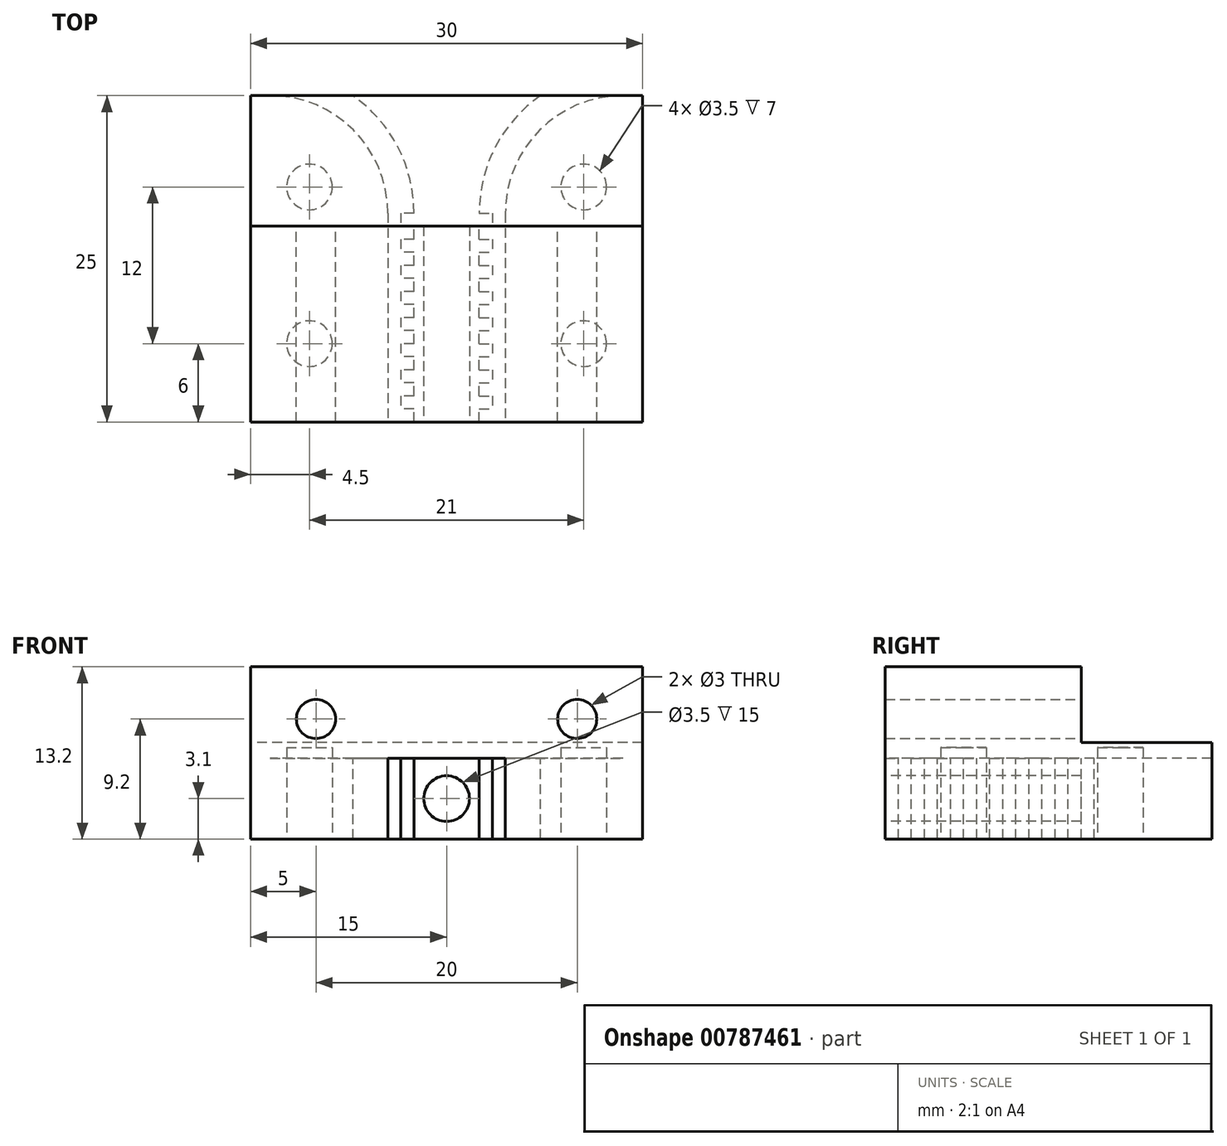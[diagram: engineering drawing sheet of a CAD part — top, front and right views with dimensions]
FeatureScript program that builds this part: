
annotation { "Feature Type Name" : "Feature", "Feature Type Description" : "" }
export const myFeature = defineFeature(function(context is Context, id is Id, definition is map)
    precondition{}
    {
        {
            var Q0;
            Q0=qCreatedBy(makeId("Front.planeOp"),FACE);
            var sketch = newSketch(context, id + "F0", { "sketchPlane" : qUnion([Q0])});
            skLineSegment(sketch, "E0.bottom", {"start": v(15, -3) * mm, "end": v(-15, -3) * mm});
            skLineSegment(sketch, "E0.top", {"start": v(15, 4) * mm, "end": v(-15, 4) * mm});
            skLineSegment(sketch, "E0.left", {"start": v(15, -3) * mm, "end": v(15, 4) * mm});
            skLineSegment(sketch, "E0.right", {"start": v(-15, -3) * mm, "end": v(-15, 4) * mm});
            skPoint(sketch, "E0.middle", {"position": v(0, 0) * mm});
            skCircle(sketch, "E1", {"center": v(-10, 0) * mm, "radius": 1.5 * mm});
            skCircle(sketch, "E2.MirrorC", {"center": v(10, 0) * mm, "radius": 1.5 * mm});
            skSolve(sketch);
        }
        {
            var Q0;
            Q0=makeQuery(id+"F0.imprint","IMPRINT",FACE,{"disambiguationData":[TD([[makeQuery(id+"F0.imprint","IMPRINT",EDGE,{"derivedFrom":sQuery(id+"F0.wireOp",EDGE,"E0.bottom")}),-1.0]])]});
            extrude(context, id + "F1", {"entities" : qUnion([Q0]), "depth" : 25 * mm, "offsetDistance" : 25 * mm});
        }
        {
            var Q0;
            Q0=makeQuery(id+"F1.opExtrude","SWEPT_FACE",FACE,{"disambiguationData":[OSD([sQuery(id+"F0.wireOp",EDGE,"E0.bottom")])]});
            var sketch = newSketch(context, id + "F2", { "sketchPlane" : qUnion([Q0])});
            skArc(sketch, "E3", {"start": v(-13.5, 0) * mm, "mid": v(-7.14, 2.64) * mm, "end": v(-4.5, 9) * mm});
            skLineSegment(sketch, "E4", {"start": v(-4.5, 9) * mm, "end": v(-4.5, 25) * mm});
            skLineSegment(sketch, "E5", {"start": v(-2.5, 25) * mm, "end": v(-2.5, 24) * mm});
            skArc(sketch, "E6", {"start": v(-7.18, 0) * mm, "mid": v(-3.74, 3.93) * mm, "end": v(-2.5, 9) * mm});
            skLineSegment(sketch, "E7", {"start": v(-13.5, 9) * mm, "end": v(4.14, 9) * mm, "construction": true});
            skLineSegment(sketch, "E8.top", {"start": v(-3.5, 23) * mm, "end": v(-3.5, 24) * mm});
            skLineSegment(sketch, "E8.left", {"start": v(-2.5, 23) * mm, "end": v(-3.5, 23) * mm});
            skLineSegment(sketch, "E8.right", {"start": v(-2.5, 24) * mm, "end": v(-3.5, 24) * mm});
            skLineSegment(sketch, "E9.1.0.0", {"start": v(-2.5, 21) * mm, "end": v(-3.5, 21) * mm});
            skLineSegment(sketch, "E9.1.0.1", {"start": v(-3.5, 21) * mm, "end": v(-3.5, 22) * mm});
            skLineSegment(sketch, "E9.1.0.2", {"start": v(-2.5, 23) * mm, "end": v(-2.5, 22) * mm});
            skLineSegment(sketch, "E9.1.0.3", {"start": v(-2.5, 22) * mm, "end": v(-3.5, 22) * mm});
            skLineSegment(sketch, "E9.2.0.0", {"start": v(-2.5, 19) * mm, "end": v(-3.5, 19) * mm});
            skLineSegment(sketch, "E9.2.0.1", {"start": v(-3.5, 19) * mm, "end": v(-3.5, 20) * mm});
            skLineSegment(sketch, "E9.2.0.2", {"start": v(-2.5, 21) * mm, "end": v(-2.5, 20) * mm});
            skLineSegment(sketch, "E9.2.0.3", {"start": v(-2.5, 20) * mm, "end": v(-3.5, 20) * mm});
            skLineSegment(sketch, "E9.3.0.0", {"start": v(-2.5, 17) * mm, "end": v(-3.5, 17) * mm});
            skLineSegment(sketch, "E9.3.0.1", {"start": v(-3.5, 17) * mm, "end": v(-3.5, 18) * mm});
            skLineSegment(sketch, "E9.3.0.2", {"start": v(-2.5, 19) * mm, "end": v(-2.5, 18) * mm});
            skLineSegment(sketch, "E9.3.0.3", {"start": v(-2.5, 18) * mm, "end": v(-3.5, 18) * mm});
            skLineSegment(sketch, "E9.4.0.0", {"start": v(-2.5, 15) * mm, "end": v(-3.5, 15) * mm});
            skLineSegment(sketch, "E9.4.0.1", {"start": v(-3.5, 15) * mm, "end": v(-3.5, 16) * mm});
            skLineSegment(sketch, "E9.4.0.2", {"start": v(-2.5, 17) * mm, "end": v(-2.5, 16) * mm});
            skLineSegment(sketch, "E9.4.0.3", {"start": v(-2.5, 16) * mm, "end": v(-3.5, 16) * mm});
            skLineSegment(sketch, "E9.5.0.0", {"start": v(-2.5, 13) * mm, "end": v(-3.5, 13) * mm});
            skLineSegment(sketch, "E9.5.0.1", {"start": v(-3.5, 13) * mm, "end": v(-3.5, 14) * mm});
            skLineSegment(sketch, "E9.5.0.2", {"start": v(-2.5, 15) * mm, "end": v(-2.5, 14) * mm});
            skLineSegment(sketch, "E9.5.0.3", {"start": v(-2.5, 14) * mm, "end": v(-3.5, 14) * mm});
            skLineSegment(sketch, "E9.6.0.0", {"start": v(-2.5, 11) * mm, "end": v(-3.5, 11) * mm});
            skLineSegment(sketch, "E9.6.0.1", {"start": v(-3.5, 11) * mm, "end": v(-3.5, 12) * mm});
            skLineSegment(sketch, "E9.6.0.2", {"start": v(-2.5, 13) * mm, "end": v(-2.5, 12) * mm});
            skLineSegment(sketch, "E9.6.0.3", {"start": v(-2.5, 12) * mm, "end": v(-3.5, 12) * mm});
            skLineSegment(sketch, "E9.7.0.0", {"start": v(-2.5, 9) * mm, "end": v(-3.5, 9) * mm});
            skLineSegment(sketch, "E9.7.0.1", {"start": v(-3.5, 9) * mm, "end": v(-3.5, 10) * mm});
            skLineSegment(sketch, "E9.7.0.2", {"start": v(-2.5, 11) * mm, "end": v(-2.5, 10) * mm});
            skLineSegment(sketch, "E9.7.0.3", {"start": v(-2.5, 10) * mm, "end": v(-3.5, 10) * mm});
            skLineSegment(sketch, "E9.direction1", {"start": v(-2.5, 23) * mm, "end": v(-2.5, 21) * mm, "construction": true});
            skLineSegment(sketch, "E10", {"start": v(0, 0) * mm, "end": v(0, 25) * mm, "construction": true});
            skLineSegment(sketch, "E11.MirrorCS", {"start": v(2.5, 23) * mm, "end": v(2.5, 22) * mm});
            skLineSegment(sketch, "E12.MirrorCS", {"start": v(2.5, 25) * mm, "end": v(2.5, 24) * mm});
            skLineSegment(sketch, "E13.MirrorCS", {"start": v(2.5, 19) * mm, "end": v(3.5, 19) * mm});
            skLineSegment(sketch, "E14.MirrorCS", {"start": v(2.5, 16) * mm, "end": v(3.5, 16) * mm});
            skLineSegment(sketch, "E15.MirrorCS", {"start": v(2.5, 18) * mm, "end": v(3.5, 18) * mm});
            skLineSegment(sketch, "E16.MirrorCS", {"start": v(2.5, 22) * mm, "end": v(3.5, 22) * mm});
            skLineSegment(sketch, "E17.MirrorCS", {"start": v(2.5, 21) * mm, "end": v(3.5, 21) * mm});
            skLineSegment(sketch, "E18.MirrorCS", {"start": v(3.5, 9) * mm, "end": v(3.5, 10) * mm});
            skLineSegment(sketch, "E19.MirrorCS", {"start": v(2.5, 24) * mm, "end": v(3.5, 24) * mm});
            skLineSegment(sketch, "E20.MirrorCS", {"start": v(2.5, 9) * mm, "end": v(3.5, 9) * mm});
            skLineSegment(sketch, "E21.MirrorCS", {"start": v(2.5, 21) * mm, "end": v(2.5, 20) * mm});
            skLineSegment(sketch, "E22.MirrorCS", {"start": v(3.5, 11) * mm, "end": v(3.5, 12) * mm});
            skLineSegment(sketch, "E23.MirrorCS", {"start": v(2.5, 12) * mm, "end": v(3.5, 12) * mm});
            skLineSegment(sketch, "E24.MirrorCS", {"start": v(2.5, 17) * mm, "end": v(2.5, 16) * mm});
            skLineSegment(sketch, "E25.MirrorCS", {"start": v(2.5, 23) * mm, "end": v(2.5, 21) * mm, "construction": true});
            skLineSegment(sketch, "E26.MirrorCS", {"start": v(2.5, 15) * mm, "end": v(3.5, 15) * mm});
            skLineSegment(sketch, "E27.MirrorCS", {"start": v(3.5, 19) * mm, "end": v(3.5, 20) * mm});
            skLineSegment(sketch, "E28.MirrorCS", {"start": v(3.5, 15) * mm, "end": v(3.5, 16) * mm});
            skLineSegment(sketch, "E29.MirrorCS", {"start": v(2.5, 19) * mm, "end": v(2.5, 18) * mm});
            skLineSegment(sketch, "E30.MirrorCS", {"start": v(3.5, 21) * mm, "end": v(3.5, 22) * mm});
            skLineSegment(sketch, "E31.MirrorCS", {"start": v(2.5, 15) * mm, "end": v(2.5, 14) * mm});
            skLineSegment(sketch, "E32.MirrorCS", {"start": v(3.5, 23) * mm, "end": v(3.5, 24) * mm});
            skLineSegment(sketch, "E33.MirrorCS", {"start": v(2.5, 13) * mm, "end": v(2.5, 12) * mm});
            skLineSegment(sketch, "E34.MirrorCS", {"start": v(2.5, 20) * mm, "end": v(3.5, 20) * mm});
            skLineSegment(sketch, "E35.MirrorCS", {"start": v(2.5, 11) * mm, "end": v(2.5, 10) * mm});
            skLineSegment(sketch, "E36.MirrorCS", {"start": v(2.5, 14) * mm, "end": v(3.5, 14) * mm});
            skLineSegment(sketch, "E37.MirrorCS", {"start": v(3.5, 13) * mm, "end": v(3.5, 14) * mm});
            skLineSegment(sketch, "E38.MirrorCS", {"start": v(2.5, 23) * mm, "end": v(3.5, 23) * mm});
            skLineSegment(sketch, "E39.MirrorCS", {"start": v(2.5, 17) * mm, "end": v(3.5, 17) * mm});
            skLineSegment(sketch, "E40.MirrorCS", {"start": v(2.5, 13) * mm, "end": v(3.5, 13) * mm});
            skLineSegment(sketch, "E41.MirrorCS", {"start": v(3.5, 17) * mm, "end": v(3.5, 18) * mm});
            skLineSegment(sketch, "E42.MirrorCS", {"start": v(2.5, 11) * mm, "end": v(3.5, 11) * mm});
            skLineSegment(sketch, "E43.MirrorCS", {"start": v(2.5, 10) * mm, "end": v(3.5, 10) * mm});
            skArc(sketch, "E44.MirrorCS", {"start": v(7.18, 0) * mm, "mid": v(3.74, 3.93) * mm, "end": v(2.5, 9) * mm});
            skLineSegment(sketch, "E45.MirrorCS", {"start": v(13.5, 9) * mm, "end": v(-4.14, 9) * mm, "construction": true});
            skLineSegment(sketch, "E46.MirrorCS", {"start": v(4.5, 9) * mm, "end": v(4.5, 25) * mm});
            skArc(sketch, "E47.MirrorCS", {"start": v(13.5, 0) * mm, "mid": v(7.14, 2.64) * mm, "end": v(4.5, 9) * mm});
            skLineSegment(sketch, "E48", {"start": v(-4.5, 25) * mm, "end": v(-15, 25) * mm});
            skLineSegment(sketch, "E49", {"start": v(-15, 25) * mm, "end": v(-15, 0) * mm});
            skLineSegment(sketch, "E50", {"start": v(-15, 0) * mm, "end": v(-13.5, 0) * mm});
            skLineSegment(sketch, "E51", {"start": v(-7.18, 0) * mm, "end": v(7.18, 0) * mm});
            skLineSegment(sketch, "E52", {"start": v(13.5, 0) * mm, "end": v(15, 0) * mm});
            skLineSegment(sketch, "E53", {"start": v(15, 0) * mm, "end": v(15, 25) * mm});
            skLineSegment(sketch, "E54", {"start": v(15, 25) * mm, "end": v(4.5, 25) * mm});
            skSolve(sketch);
        }
        {
            var Q0;
            {var subQ1=sQuery(id+"F2.wireOp",EDGE,"E5");Q0=makeQuery(id+"F2.imprint","IMPRINT",FACE,{"disambiguationData":[TD([[makeQuery(id+"F2.imprint","IMPRINT",EDGE,{"derivedFrom":subQ1}),1.0]])]});}
            extrude(context, id + "F3", {"entities" : qUnion([Q0]), "depth" : 6.2 * mm, "offsetDistance" : 25 * mm});
        }
        {
            var Q0;
            Q0 = qSketchRegion(id + "F2", true);
            extrude(context, id + "F4", {"entities" : qUnion([Q0]), "operationType" : NewBodyOperationType.ADD, "depth" : 6.2 * mm, "offsetDistance" : 25 * mm});
        }
        {
            var Q0;
            Q0=makeQuery(id+"F3.opExtrude","SWEPT_FACE",FACE,{"disambiguationData":[OSD([sQuery(id+"F0.wireOp",EDGE,"E0.bottom")])]});
            var sketch = newSketch(context, id + "F5", { "sketchPlane" : qUnion([Q0])});
            skLineSegment(sketch, "E55", {"start": v(0, -3) * mm, "end": v(0, -9.2) * mm, "construction": true});
            skLineSegment(sketch, "E56", {"start": v(0, -9.2) * mm, "end": v(-0.2, -9.17) * mm, "construction": true});
            skLineSegment(sketch, "E57", {"start": v(-2.5, -6.1) * mm, "end": v(2.5, -6.1) * mm, "construction": true});
            skCircle(sketch, "E58", {"center": v(0, -6.1) * mm, "radius": 1.75 * mm});
            skSolve(sketch);
        }
        {
            var Q0;
            Q0=makeQuery(id+"F5.imprint","IMPRINT",FACE,{"disambiguationData":[TD([[makeQuery(id+"F5.imprint","IMPRINT",EDGE,{"derivedFrom":sQuery(id+"F5.wireOp",EDGE,"E58")}),1.0]])]});
            extrude(context, id + "F6", {"entities" : qUnion([Q0]), "operationType" : NewBodyOperationType.REMOVE, "oppositeDirection" : true, "depth" : 15 * mm, "offsetDistance" : 25 * mm});
        }
        {
            var Q0;
            Q0=makeQuery(id+"F4.opExtrude","CAP_FACE",FACE,{"disambiguationData":[OSD([sQuery(id+"F2.wireOp",EDGE,"E46.MirrorCS"),sQuery(id+"F2.wireOp",EDGE,"E47.MirrorCS"),sQuery(id+"F2.wireOp",EDGE,"E52"),sQuery(id+"F2.wireOp",EDGE,"E53"),sQuery(id+"F2.wireOp",EDGE,"E54")])],"isStart":false});
            var sketch = newSketch(context, id + "F7", { "sketchPlane" : qUnion([Q0])});
            skLineSegment(sketch, "E59", {"start": v(10.5, 3.36) * mm, "end": v(10.5, 25.43) * mm, "construction": true});
            skCircle(sketch, "E60", {"center": v(10.5, 7) * mm, "radius": 1.75 * mm});
            skCircle(sketch, "E61", {"center": v(10.5, 19) * mm, "radius": 1.75 * mm});
            skCircle(sketch, "E62.MirrorC", {"center": v(-10.5, 7) * mm, "radius": 1.75 * mm});
            skCircle(sketch, "E63.MirrorC", {"center": v(-10.5, 19) * mm, "radius": 1.75 * mm});
            skSolve(sketch);
        }
        {
            var Q0;
            Q0 = qSketchRegion(id + "F7", true);
            extrude(context, id + "F8", {"entities" : qUnion([Q0]), "operationType" : NewBodyOperationType.REMOVE, "oppositeDirection" : true, "depth" : 7 * mm, "offsetDistance" : 25 * mm});
        }
        {
            var Q0;
            Q0=makeQuery(id+"F4.boolean.opBoolean","MERGE",FACE,{"derivedFrom":[makeQuery(id+"F1.opExtrude","CAP_FACE",FACE,{"disambiguationData":[OSD([sQuery(id+"F0.wireOp",EDGE,"E0.bottom"),sQuery(id+"F0.wireOp",EDGE,"E0.top"),sQuery(id+"F0.wireOp",EDGE,"E0.left"),sQuery(id+"F0.wireOp",EDGE,"E0.right"),sQuery(id+"F0.wireOp",EDGE,"E1"),sQuery(id+"F0.wireOp",EDGE,"E2.MirrorC")])],"isStart":true}),makeQuery(id+"F4.opExtrude","SWEPT_FACE",FACE,{"disambiguationData":[OSD([sQuery(id+"F2.wireOp",EDGE,"E50")])]}),makeQuery(id+"F4.opExtrude","SWEPT_FACE",FACE,{"disambiguationData":[OSD([sQuery(id+"F2.wireOp",EDGE,"E52")])]})]});
            var sketch = newSketch(context, id + "F9", { "sketchPlane" : qUnion([Q0])});
            skLineSegment(sketch, "E64.bottom", {"start": v(-15, 4) * mm, "end": v(15, 4) * mm});
            skLineSegment(sketch, "E64.top", {"start": v(-15, -1.8) * mm, "end": v(15, -1.8) * mm});
            skLineSegment(sketch, "E64.left", {"start": v(-15, 4) * mm, "end": v(-15, -1.8) * mm});
            skLineSegment(sketch, "E64.right", {"start": v(15, 4) * mm, "end": v(15, -1.8) * mm});
            skSolve(sketch);
        }
        {
            var Q0;
            Q0=makeQuery(id+"F9.imprint","IMPRINT",FACE,{"disambiguationData":[TD([[makeQuery(id+"F9.imprint","IMPRINT",EDGE,{"derivedFrom":sQuery(id+"F9.wireOp",EDGE,"E64.bottom")}),-1.0]])]});
            extrude(context, id + "F10", {"entities" : qUnion([Q0]), "operationType" : NewBodyOperationType.REMOVE, "oppositeDirection" : true, "depth" : 10 * mm, "offsetDistance" : 25 * mm});
        }
    });
